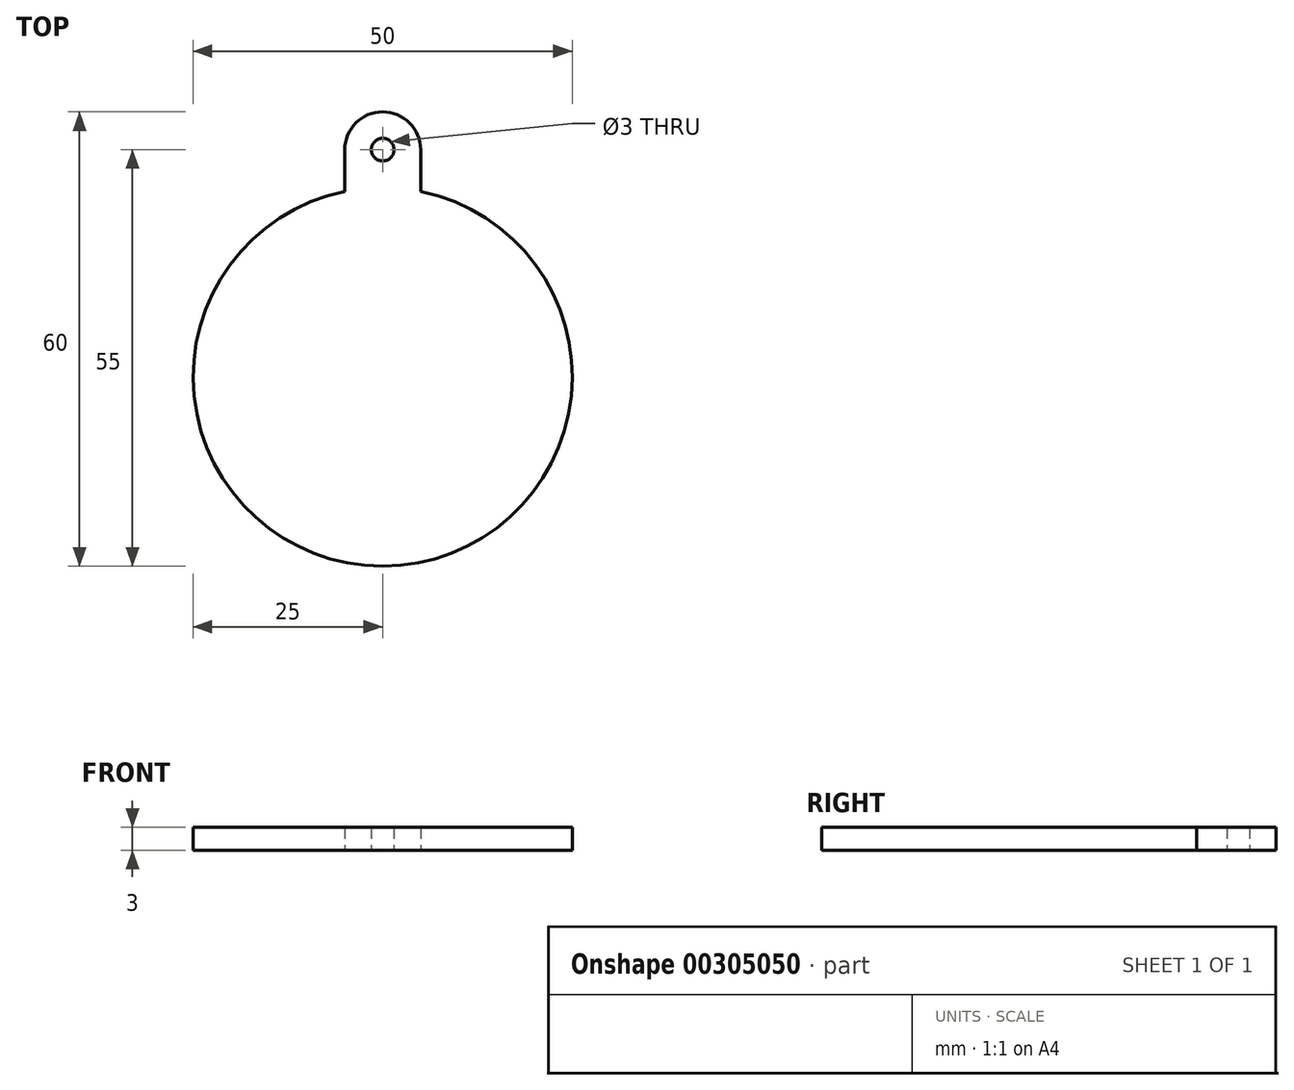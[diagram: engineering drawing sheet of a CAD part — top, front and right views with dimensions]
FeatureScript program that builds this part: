
annotation { "Feature Type Name" : "Feature", "Feature Type Description" : "" }
export const myFeature = defineFeature(function(context is Context, id is Id, definition is map)
    precondition{}
    {
        {
            var Q0;
            Q0=qCreatedBy(makeId("Top.planeOp"),FACE);
            var sketch = newSketch(context, id + "F0", { "sketchPlane" : qUnion([Q0])});
            skArc(sketch, "E0", {"start": v(-5, 24.5) * mm, "mid": v(0, -25) * mm, "end": v(5, 24.5) * mm});
            skCircle(sketch, "E1", {"center": v(0, 30) * mm, "radius": 1.5 * mm});
            skArc(sketch, "E2", {"start": v(5, 30) * mm, "mid": v(0, 35) * mm, "end": v(-5, 30) * mm});
            skLineSegment(sketch, "E3", {"start": v(-5, 30) * mm, "end": v(-5, 24.5) * mm});
            skLineSegment(sketch, "E4", {"start": v(5, 30) * mm, "end": v(5, 24.5) * mm});
            skSolve(sketch);
        }
        {
            var Q0;
            Q0 = qSketchRegion(id + "F0", true);
            extrude(context, id + "F1", {"entities" : qUnion([Q0]), "depth" : 3 * mm});
        }
    });
